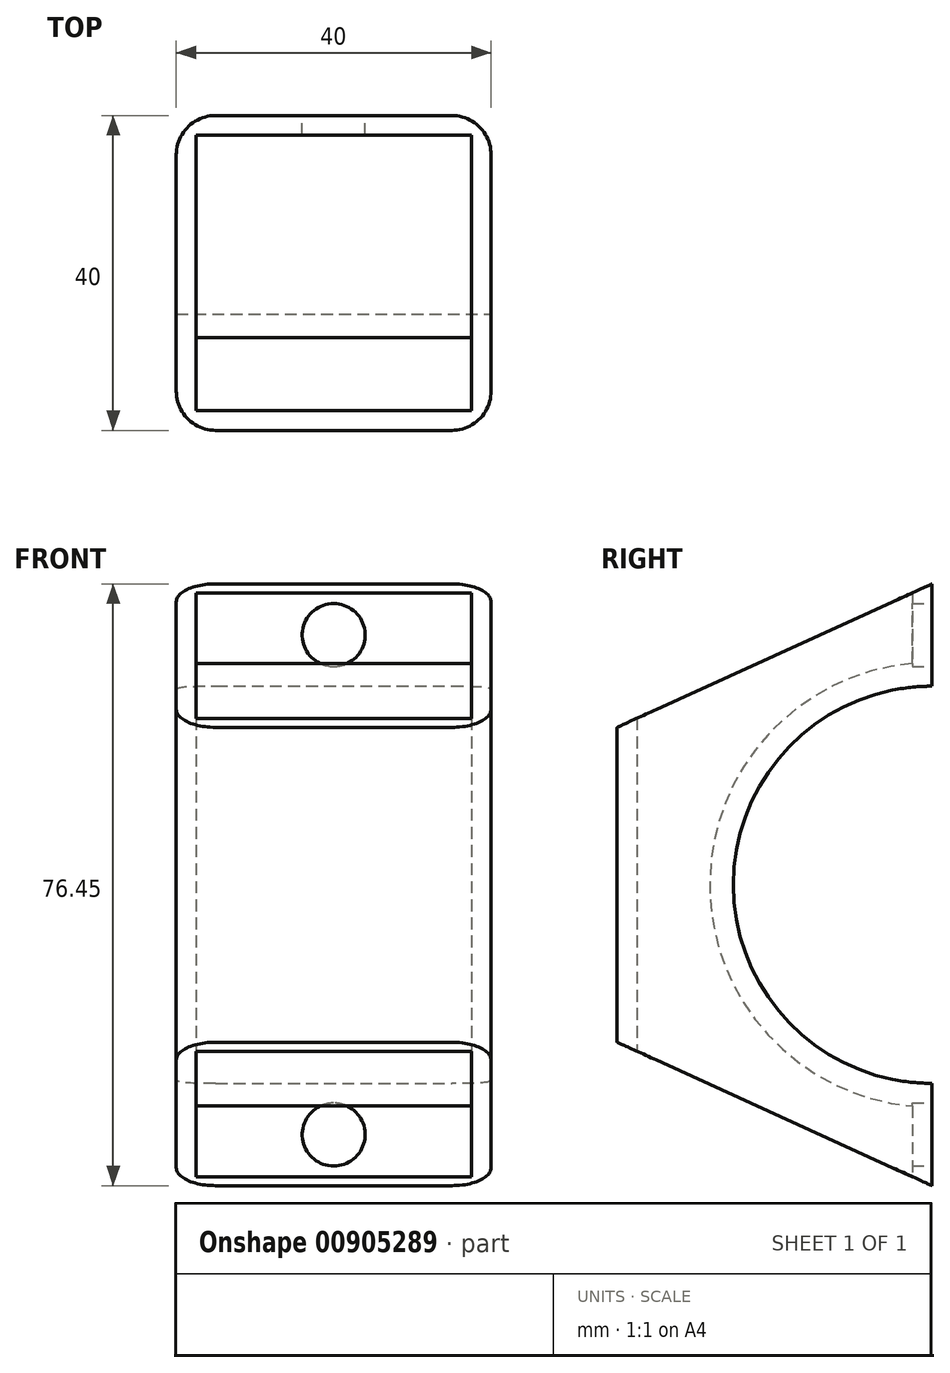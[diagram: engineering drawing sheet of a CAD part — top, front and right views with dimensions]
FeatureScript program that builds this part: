
annotation { "Feature Type Name" : "Feature", "Feature Type Description" : "" }
export const myFeature = defineFeature(function(context is Context, id is Id, definition is map)
    precondition{}
    {
        {
            var Q0;
            Q0=qCreatedBy(makeId("Top.planeOp"),FACE);
            var sketch = newSketch(context, id + "F0", { "sketchPlane" : qUnion([Q0])});
            skLineSegment(sketch, "E0.bottom", {"start": v(-20, 20) * mm, "end": v(20, 20) * mm});
            skLineSegment(sketch, "E0.top", {"start": v(-20, -20) * mm, "end": v(20, -20) * mm});
            skLineSegment(sketch, "E0.left", {"start": v(-20, 20) * mm, "end": v(-20, -20) * mm});
            skLineSegment(sketch, "E0.right", {"start": v(20, 20) * mm, "end": v(20, -20) * mm});
            skLineSegment(sketch, "E1.bottom", {"start": v(-17.5, 17.5) * mm, "end": v(17.5, 17.5) * mm});
            skLineSegment(sketch, "E1.top", {"start": v(-17.5, -17.5) * mm, "end": v(17.5, -17.5) * mm});
            skLineSegment(sketch, "E1.left", {"start": v(-17.5, 17.5) * mm, "end": v(-17.5, -17.5) * mm});
            skLineSegment(sketch, "E1.right", {"start": v(17.5, 17.5) * mm, "end": v(17.5, -17.5) * mm});
            skSolve(sketch);
        }
        {
            var Q0;
            Q0 = qSketchRegion(id + "F0", true);
            extrude(context, id + "F1", {"entities" : qUnion([Q0]), "depth" : 100 * mm, "offsetDistance" : 25 * mm});
        }
        {
            var Q0;
            Q0=makeQuery(id+"F1.opExtrude","SWEPT_FACE",FACE,{"disambiguationData":[OSD([sQuery(id+"F0.wireOp",EDGE,"E0.right")])]});
            var sketch = newSketch(context, id + "F2", { "sketchPlane" : qUnion([Q0])});
            skArc(sketch, "E2", {"start": v(20, 75.8) * mm, "mid": v(-5.23, 50.57) * mm, "end": v(20, 25.34) * mm});
            skArc(sketch, "E3", {"start": v(20, 78.8) * mm, "mid": v(-8.23, 50.57) * mm, "end": v(20, 22.34) * mm});
            skLineSegment(sketch, "E4", {"start": v(20, 78.8) * mm, "end": v(20, 22.34) * mm});
            skLineSegment(sketch, "E5", {"start": v(-20, 70.57) * mm, "end": v(-20, 30.57) * mm});
            skLineSegment(sketch, "E6", {"start": v(20, 22.34) * mm, "end": v(20, 12.34) * mm});
            skLineSegment(sketch, "E7", {"start": v(20, 12.34) * mm, "end": v(-20, 30.57) * mm});
            skLineSegment(sketch, "E8", {"start": v(20, 78.8) * mm, "end": v(20, 88.8) * mm});
            skLineSegment(sketch, "E9", {"start": v(20, 88.8) * mm, "end": v(-20, 70.57) * mm});
            skSolve(sketch);
        }
        {
            var Q0;
            {var subQ0=sQuery(id+"F2.wireOp",EDGE,"E2");Q0=makeQuery(id+"F2.imprint","IMPRINT",FACE,{"disambiguationData":[TD([[makeQuery(id+"F2.imprint","IMPRINT",EDGE,{"derivedFrom":subQ0}),1.0]])]});}
            var Q1;
            {var subQ0=sQuery(id+"F2.wireOp",EDGE,"E2");Q1=makeQuery(id+"F2.imprint","IMPRINT",FACE,{"disambiguationData":[TD([[makeQuery(id+"F2.imprint","IMPRINT",EDGE,{"derivedFrom":subQ0}),-1.0]])]});}
            var Q2;
            {var subQ0=sQuery(id+"F2.wireOp",EDGE,"E7");Q2=makeQuery(id+"F2.imprint","IMPRINT",FACE,{"disambiguationData":[TD([[makeQuery(id+"F2.imprint","IMPRINT",EDGE,{"derivedFrom":subQ0}),1.0]])]});}
            var Q3;
            {var subQ0=sQuery(id+"F2.wireOp",EDGE,"E9");Q3=makeQuery(id+"F2.imprint","IMPRINT",FACE,{"disambiguationData":[TD([[makeQuery(id+"F2.imprint","IMPRINT",EDGE,{"derivedFrom":subQ0}),-1.0]])]});}
            extrude(context, id + "F3", {"entities" : qUnion([Q0, Q1, Q2, Q3]), "operationType" : NewBodyOperationType.REMOVE, "endBound" : BoundingType.THROUGH_ALL, "oppositeDirection" : true, "depth" : 25 * mm, "offsetDistance" : 25 * mm});
        }
        {
            var Q0;
            {var subQ0=sQuery(id+"F2.wireOp",EDGE,"E2");Q0=makeQuery(id+"F2.imprint","IMPRINT",FACE,{"disambiguationData":[TD([[makeQuery(id+"F2.imprint","IMPRINT",EDGE,{"derivedFrom":subQ0}),-1.0]])]});}
            extrude(context, id + "F4", {"entities" : qUnion([Q0]), "operationType" : NewBodyOperationType.ADD, "oppositeDirection" : true, "depth" : 40 * mm, "offsetDistance" : 25 * mm});
        }
        {
            var Q0;
            {var subQ0=sQuery(id+"F2.wireOp",EDGE,"E4");Q0=makeQuery(id+"F4.boolean.opBoolean","MERGE",FACE,{"derivedFrom":[makeQuery(id+"F3.boolean.opBoolean","SPLIT",FACE,{"disambiguationData":[TD([makeQuery(id+"F3.opExtrude","SWEPT_FACE",FACE,{"disambiguationData":[OSD([sQuery(id+"F2.wireOp",EDGE,"E9")])]})])],"derivedFrom":makeQuery(id+"F1.opExtrude","SWEPT_FACE",FACE,{"disambiguationData":[OSD([sQuery(id+"F0.wireOp",EDGE,"E0.bottom")])]})}),makeQuery(id+"F4.opExtrude","SWEPT_FACE",FACE,{"disambiguationData":[OSD([subQ0]),TDD([makeQuery(id+"F2.imprint","IMPRINT",EDGE,{"disambiguationData":[TD([[makeQuery(id+"F2.imprint","INTERSECT",VERTEX,{"disambiguationData":[OD(0.0)],"derivedFrom":[sQuery(id+"F2.wireOp",EDGE,"E2"),subQ0]}),1.0]])],"derivedFrom":subQ0})])]})]});}
            var sketch = newSketch(context, id + "F5", { "sketchPlane" : qUnion([Q0])});
            skCircle(sketch, "E10", {"center": v(0, 82.3) * mm, "radius": 4 * mm});
            skSolve(sketch);
        }
        {
            var Q0;
            Q0 = qSketchRegion(id + "F5", true);
            extrude(context, id + "F6", {"entities" : qUnion([Q0]), "operationType" : NewBodyOperationType.REMOVE, "oppositeDirection" : true, "depth" : 2.5 * mm, "offsetDistance" : 25 * mm});
        }
        {
            var Q0;
            {var subQ0=sQuery(id+"F2.wireOp",EDGE,"E4");Q0=makeQuery(id+"F4.boolean.opBoolean","MERGE",FACE,{"derivedFrom":[makeQuery(id+"F3.boolean.opBoolean","SPLIT",FACE,{"disambiguationData":[TD([makeQuery(id+"F3.opExtrude","SWEPT_FACE",FACE,{"disambiguationData":[OSD([sQuery(id+"F2.wireOp",EDGE,"E7")])]})])],"derivedFrom":makeQuery(id+"F1.opExtrude","SWEPT_FACE",FACE,{"disambiguationData":[OSD([sQuery(id+"F0.wireOp",EDGE,"E0.bottom")])]})}),makeQuery(id+"F4.opExtrude","SWEPT_FACE",FACE,{"disambiguationData":[OSD([subQ0]),TDD([makeQuery(id+"F2.imprint","IMPRINT",EDGE,{"disambiguationData":[TD([[makeQuery(id+"F2.imprint","INTERSECT",VERTEX,{"disambiguationData":[OD(1.0)],"derivedFrom":[sQuery(id+"F2.wireOp",EDGE,"E2"),subQ0]}),-1.0]])],"derivedFrom":subQ0})])]})]});}
            var sketch = newSketch(context, id + "F7", { "sketchPlane" : qUnion([Q0])});
            skLineSegment(sketch, "E11", {"start": v(0, 12.34) * mm, "end": v(0, 25.34) * mm});
            skCircle(sketch, "E12", {"center": v(0, 18.84) * mm, "radius": 4 * mm});
            skSolve(sketch);
        }
        {
            var Q0;
            Q0 = qSketchRegion(id + "F7", true);
            extrude(context, id + "F8", {"entities" : qUnion([Q0]), "operationType" : NewBodyOperationType.REMOVE, "oppositeDirection" : true, "depth" : 2.5 * mm, "offsetDistance" : 25 * mm});
        }
        {
            var Q0;
            {var subQ0=sQuery(id+"F2.wireOp",EDGE,"E4");var subQ2=sQuery(id+"F0.wireOp",EDGE,"E0.bottom");var subQ3=sQuery(id+"F0.wireOp",EDGE,"E0.left");Q0=makeQuery(id+"F4.boolean.opBoolean","MERGE",EDGE,{"derivedFrom":[makeQuery(id+"F3.boolean.opBoolean","SPLIT",EDGE,{"disambiguationData":[TD([makeQuery(id+"F3.opExtrude","SWEPT_FACE",FACE,{"disambiguationData":[OSD([sQuery(id+"F2.wireOp",EDGE,"E9")])]})])],"derivedFrom":makeQuery(id+"F1.opExtrude","SWEPT_EDGE",EDGE,{"disambiguationData":[OSD([subQ2,subQ3])]})}),makeQuery(id+"F4.opExtrude","CAP_EDGE",EDGE,{"disambiguationData":[OSD([subQ0]),TDD([makeQuery(id+"F2.imprint","IMPRINT",EDGE,{"disambiguationData":[TD([[makeQuery(id+"F2.imprint","INTERSECT",VERTEX,{"disambiguationData":[OD(0.0)],"derivedFrom":[sQuery(id+"F2.wireOp",EDGE,"E2"),subQ0]}),1.0]])],"derivedFrom":subQ0})])],"isStart":false})]});}
            var Q1;
            {var subQ0=sQuery(id+"F2.wireOp",EDGE,"E4");var subQ2=sQuery(id+"F0.wireOp",EDGE,"E0.bottom");var subQ3=sQuery(id+"F0.wireOp",EDGE,"E0.left");Q1=makeQuery(id+"F4.boolean.opBoolean","MERGE",EDGE,{"derivedFrom":[makeQuery(id+"F3.boolean.opBoolean","SPLIT",EDGE,{"disambiguationData":[TD([makeQuery(id+"F3.opExtrude","SWEPT_FACE",FACE,{"disambiguationData":[OSD([sQuery(id+"F2.wireOp",EDGE,"E7")])]})])],"derivedFrom":makeQuery(id+"F1.opExtrude","SWEPT_EDGE",EDGE,{"disambiguationData":[OSD([subQ2,subQ3])]})}),makeQuery(id+"F4.opExtrude","CAP_EDGE",EDGE,{"disambiguationData":[OSD([subQ0]),TDD([makeQuery(id+"F2.imprint","IMPRINT",EDGE,{"disambiguationData":[TD([[makeQuery(id+"F2.imprint","INTERSECT",VERTEX,{"disambiguationData":[OD(1.0)],"derivedFrom":[sQuery(id+"F2.wireOp",EDGE,"E2"),subQ0]}),-1.0]])],"derivedFrom":subQ0})])],"isStart":false})]});}
            var Q2;
            Q2=makeQuery(id+"F1.opExtrude","SWEPT_EDGE",EDGE,{"disambiguationData":[OSD([sQuery(id+"F0.wireOp",EDGE,"E0.top"),sQuery(id+"F0.wireOp",EDGE,"E0.left")])]});
            var Q3;
            Q3=makeQuery(id+"F1.opExtrude","SWEPT_EDGE",EDGE,{"disambiguationData":[OSD([sQuery(id+"F0.wireOp",EDGE,"E0.top"),sQuery(id+"F0.wireOp",EDGE,"E0.right")])]});
            var Q4;
            {var subQ0=sQuery(id+"F2.wireOp",EDGE,"E4");var subQ2=sQuery(id+"F0.wireOp",EDGE,"E0.bottom");var subQ3=sQuery(id+"F0.wireOp",EDGE,"E0.right");Q4=makeQuery(id+"F4.boolean.opBoolean","MERGE",EDGE,{"derivedFrom":[makeQuery(id+"F3.boolean.opBoolean","SPLIT",EDGE,{"disambiguationData":[TD([makeQuery(id+"F3.opExtrude","SWEPT_FACE",FACE,{"disambiguationData":[OSD([sQuery(id+"F2.wireOp",EDGE,"E7")])]})])],"derivedFrom":makeQuery(id+"F1.opExtrude","SWEPT_EDGE",EDGE,{"disambiguationData":[OSD([subQ2,subQ3])]})}),makeQuery(id+"F4.opExtrude","CAP_EDGE",EDGE,{"disambiguationData":[OSD([subQ0]),TDD([makeQuery(id+"F2.imprint","IMPRINT",EDGE,{"disambiguationData":[TD([[makeQuery(id+"F2.imprint","INTERSECT",VERTEX,{"disambiguationData":[OD(1.0)],"derivedFrom":[sQuery(id+"F2.wireOp",EDGE,"E2"),subQ0]}),-1.0]])],"derivedFrom":subQ0})])],"isStart":true})]});}
            var Q5;
            {var subQ0=sQuery(id+"F2.wireOp",EDGE,"E4");var subQ2=sQuery(id+"F0.wireOp",EDGE,"E0.bottom");var subQ3=sQuery(id+"F0.wireOp",EDGE,"E0.right");Q5=makeQuery(id+"F4.boolean.opBoolean","MERGE",EDGE,{"derivedFrom":[makeQuery(id+"F3.boolean.opBoolean","SPLIT",EDGE,{"disambiguationData":[TD([makeQuery(id+"F3.opExtrude","SWEPT_FACE",FACE,{"disambiguationData":[OSD([sQuery(id+"F2.wireOp",EDGE,"E9")])]})])],"derivedFrom":makeQuery(id+"F1.opExtrude","SWEPT_EDGE",EDGE,{"disambiguationData":[OSD([subQ2,subQ3])]})}),makeQuery(id+"F4.opExtrude","CAP_EDGE",EDGE,{"disambiguationData":[OSD([subQ0]),TDD([makeQuery(id+"F2.imprint","IMPRINT",EDGE,{"disambiguationData":[TD([[makeQuery(id+"F2.imprint","INTERSECT",VERTEX,{"disambiguationData":[OD(0.0)],"derivedFrom":[sQuery(id+"F2.wireOp",EDGE,"E2"),subQ0]}),1.0]])],"derivedFrom":subQ0})])],"isStart":true})]});}
            fillet(context, id + "F9", {"entities" : qUnion([Q0, Q1, Q2, Q3, Q4, Q5]), "radius" : 5 * mm, "tangentPropagation" : true, "allowEdgeOverflow" : false});
        }
    });
